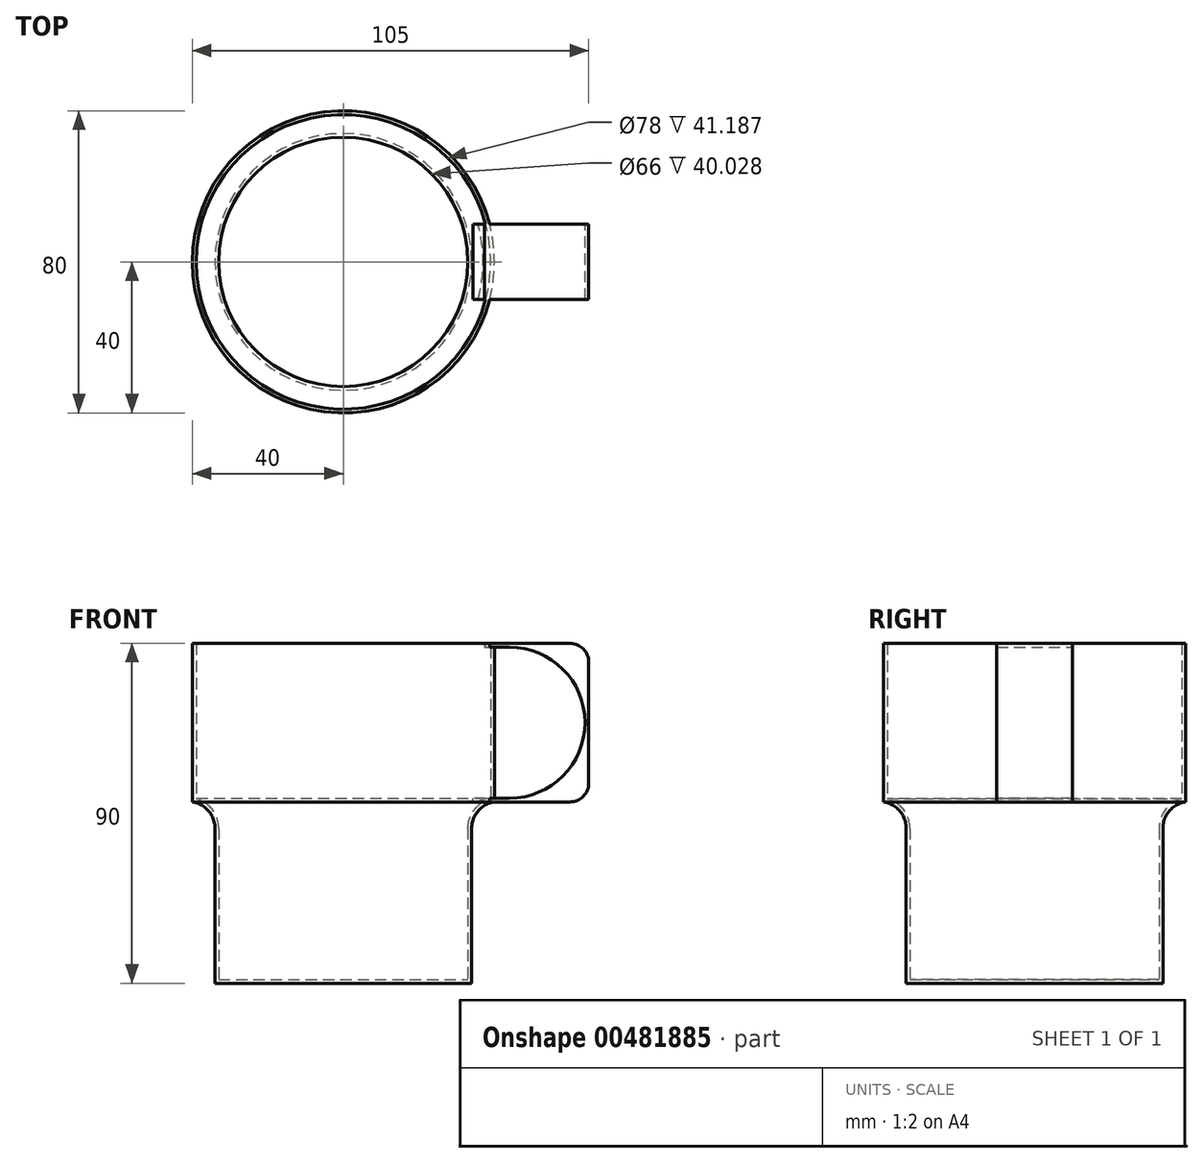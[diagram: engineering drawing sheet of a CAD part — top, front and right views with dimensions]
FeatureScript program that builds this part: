
annotation { "Feature Type Name" : "Feature", "Feature Type Description" : "" }
export const myFeature = defineFeature(function(context is Context, id is Id, definition is map)
    precondition{}
    {
        {
            var Q0;
            Q0=qCreatedBy(makeId("Front.planeOp"),FACE);
            var sketch = newSketch(context, id + "F0", { "sketchPlane" : qUnion([Q0])});
            skLineSegment(sketch, "E0", {"start": v(0, 0) * mm, "end": v(0, 90) * mm});
            skLineSegment(sketch, "E1", {"start": v(0, 0) * mm, "end": v(-34, 0) * mm});
            skLineSegment(sketch, "E2", {"start": v(-34, 0) * mm, "end": v(-34, 41.03) * mm});
            skArc(sketch, "E3", {"start": v(-34, 41.03) * mm, "mid": v(-35.7, 45.63) * mm, "end": v(-40, 48) * mm});
            skLineSegment(sketch, "E4", {"start": v(-40, 48) * mm, "end": v(-40, 90) * mm});
            skLineSegment(sketch, "E5", {"start": v(-40, 90) * mm, "end": v(0, 90) * mm});
            skSolve(sketch);
        }
        {
            var Q0;
            Q0 = qSketchRegion(id + "F0", true);
            var Q1;
            Q1=sQuery(id+"F0.wireOp",EDGE,"E0");
            revolve(context, id + "F1", {"entities" : qUnion([Q0]), "axis" : qUnion([Q1]), "revolveType" : RevolveType.FULL});
        }
        {
            var Q0;
            Q0=makeQuery(id+"F1.opRevolve","SWEPT_FACE",FACE,{"disambiguationData":[OSD([sQuery(id+"F0.wireOp",EDGE,"E5")])]});
            shell(context, id + "F2", {"entities" : qUnion([Q0]), "thickness" : 1 * mm});
        }
        {
            var Q0;
            Q0=qCreatedBy(makeId("Front.planeOp"),FACE);
            var sketch = newSketch(context, id + "F3", { "sketchPlane" : qUnion([Q0])});
            skLineSegment(sketch, "E6", {"start": v(37.4, 90) * mm, "end": v(60, 90) * mm});
            skLineSegment(sketch, "E7", {"start": v(65, 85) * mm, "end": v(65, 53) * mm});
            skLineSegment(sketch, "E8", {"start": v(60, 48) * mm, "end": v(34.3, 48) * mm});
            skPoint(sketch, "E9.visualSharp", {"position": v(65, 90) * mm});
            skArc(sketch, "E9.filletArc", {"start": v(65, 85) * mm, "mid": v(63.54, 88.54) * mm, "end": v(60, 90) * mm});
            skPoint(sketch, "E10.visualSharp", {"position": v(65, 48) * mm});
            skArc(sketch, "E10.filletArc", {"start": v(60, 48) * mm, "mid": v(63.54, 49.46) * mm, "end": v(65, 53) * mm});
            skLineSegment(sketch, "E11.0", {"start": v(44, 49) * mm, "end": v(34.3, 49) * mm});
            skLineSegment(sketch, "E11.1", {"start": v(64, 69) * mm, "end": v(64, 69) * mm});
            skLineSegment(sketch, "E11.2", {"start": v(37.4, 89) * mm, "end": v(44, 89) * mm});
            skPoint(sketch, "E12.visualSharp", {"position": v(64, 89) * mm});
            skArc(sketch, "E12.filletArc", {"start": v(64, 69) * mm, "mid": v(58.14, 83.14) * mm, "end": v(44, 89) * mm});
            skPoint(sketch, "E13.visualSharp", {"position": v(64, 49) * mm});
            skArc(sketch, "E13.filletArc", {"start": v(44, 49) * mm, "mid": v(58.14, 54.86) * mm, "end": v(64, 69) * mm});
            skLineSegment(sketch, "E14", {"start": v(37.4, 90) * mm, "end": v(37.4, 89) * mm});
            skLineSegment(sketch, "E15", {"start": v(34.3, 48) * mm, "end": v(34.3, 49) * mm});
            skSolve(sketch);
        }
        {
            var Q0;
            Q0 = qSketchRegion(id + "F3", true);
            extrude(context, id + "F4", {"entities" : qUnion([Q0]), "operationType" : NewBodyOperationType.ADD, "endBound" : BoundingType.SYMMETRIC, "depth" : 20 * mm});
        }
    });
